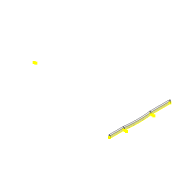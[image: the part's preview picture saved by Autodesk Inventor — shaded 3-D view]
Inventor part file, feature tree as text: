
AUTODESK INVENTOR PART (.ipt)
format: ipt  version: 2022 (Build 260153000, 153)  size: 125,952 bytes
history: native  units: mm
features: sketch x2, extrude x1, other x1, fillet x1, projected_geometry x1
ambient origin geometry x8: Origin, YZ Plane, XZ Plane, XY Plane, X Axis, Y Axis, Z Axis, Center Point
bodies: Solid1 (feature_tree)
feature tree (6):
  extrude  "Extrusion1"  Depth=6.0mm
  other  "Work Axis1"
  fillet  "Fillet1"  Radius=3.0mm
  sketch  "Sketch2"  dims[d3=3.0mm d4=8.0mm d5=0.0mm d6=3.0mm d7=158.374mm d8=3.0mm d9=53.738mm d10=400.0mm d11=400.0mm d12=10.0mm]
  sketch  "Sketch1"  dims[d0=233.87mm d1=6.0mm d2=3.0mm]
  projected_geometry  "Projected Loop1"
